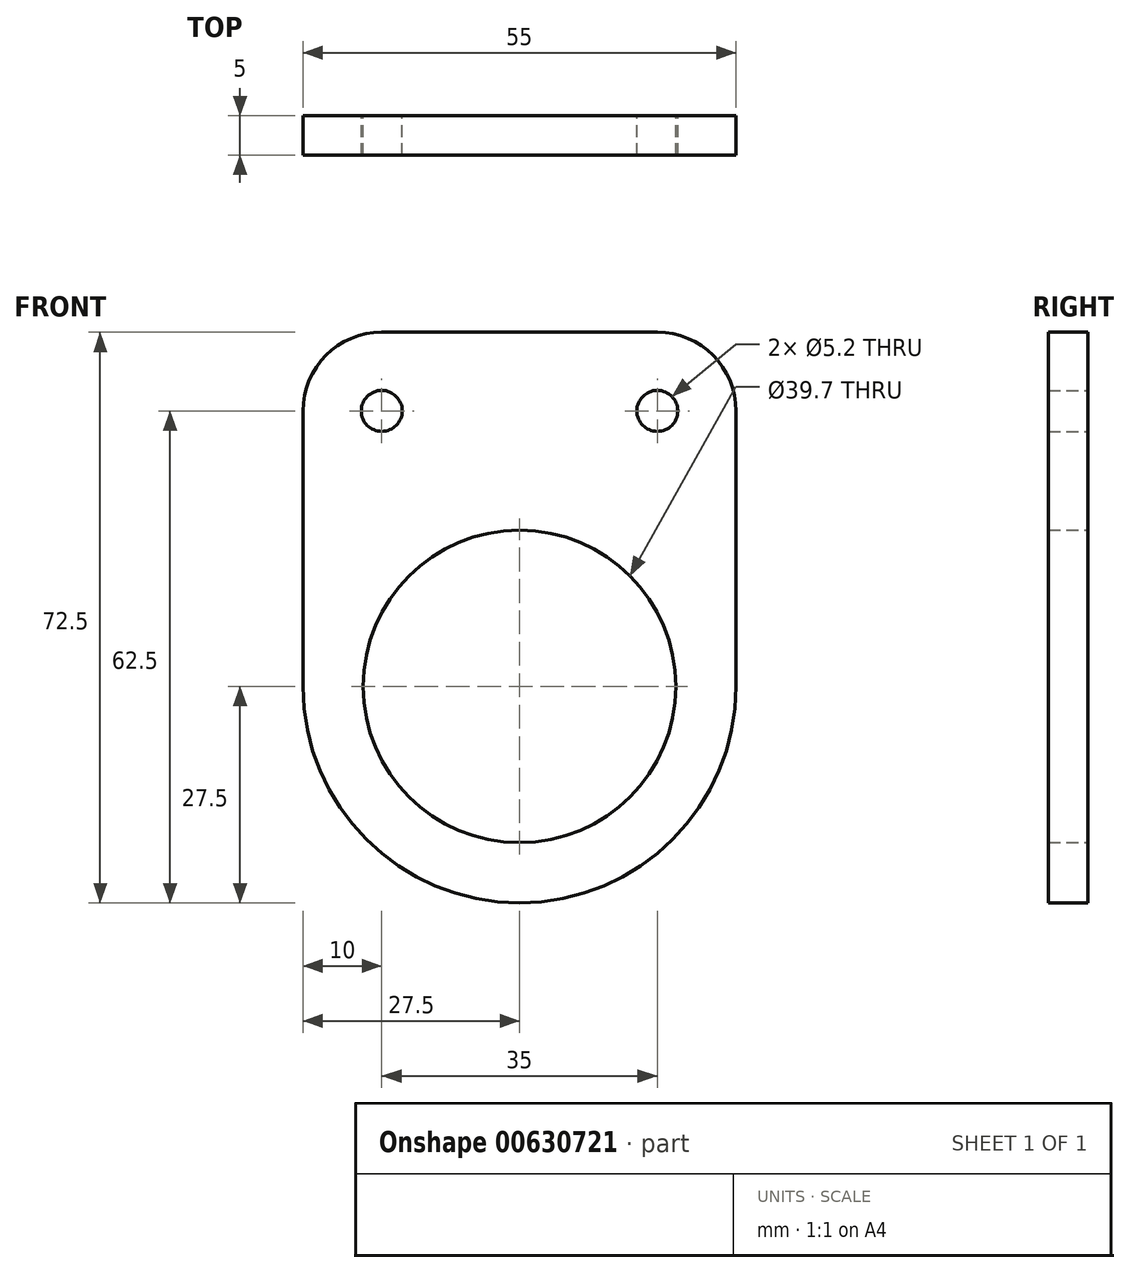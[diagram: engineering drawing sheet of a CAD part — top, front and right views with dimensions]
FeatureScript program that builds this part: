
annotation { "Feature Type Name" : "Feature", "Feature Type Description" : "" }
export const myFeature = defineFeature(function(context is Context, id is Id, definition is map)
    precondition{}
    {
        {
            var Q0;
            Q0=qCreatedBy(makeId("Front.planeOp"),FACE);
            var sketch = newSketch(context, id + "F0", { "sketchPlane" : qUnion([Q0])});
            skCircle(sketch, "E0", {"center": v(0, 0) * mm, "radius": 19.85 * mm});
            skArc(sketch, "E1", {"start": v(-27.5, 0) * mm, "mid": v(0, -27.5) * mm, "end": v(27.5, 0) * mm});
            skLineSegment(sketch, "E2.top", {"start": v(-17.5, 45) * mm, "end": v(17.5, 45) * mm});
            skLineSegment(sketch, "E2.left", {"start": v(-27.5, 0) * mm, "end": v(-27.5, 35) * mm});
            skLineSegment(sketch, "E2.right", {"start": v(27.5, 0) * mm, "end": v(27.5, 35) * mm});
            skLineSegment(sketch, "E3", {"start": v(-27.5, 35) * mm, "end": v(27.5, 35) * mm, "construction": true});
            skCircle(sketch, "E4", {"center": v(-17.5, 35) * mm, "radius": 2.6 * mm});
            skCircle(sketch, "E5", {"center": v(17.5, 35) * mm, "radius": 2.6 * mm});
            skPoint(sketch, "E6.visualSharp", {"position": v(-27.5, 45) * mm});
            skArc(sketch, "E6.filletArc", {"start": v(-17.5, 45) * mm, "mid": v(-24.57, 42.07) * mm, "end": v(-27.5, 35) * mm});
            skPoint(sketch, "E7.visualSharp", {"position": v(27.5, 45) * mm});
            skArc(sketch, "E7.filletArc", {"start": v(27.5, 35) * mm, "mid": v(24.57, 42.07) * mm, "end": v(17.5, 45) * mm});
            skLineSegment(sketch, "E8", {"start": v(-27.5, 25) * mm, "end": v(27.5, 25) * mm, "construction": true});
            skSolve(sketch);
        }
        {
            var Q0;
            Q0=makeQuery(id+"F0.imprint","IMPRINT",FACE,{"disambiguationData":[TD([[makeQuery(id+"F0.imprint","IMPRINT",EDGE,{"derivedFrom":sQuery(id+"F0.wireOp",EDGE,"E0")}),-1.0]])]});
            extrude(context, id + "F1", {"entities" : qUnion([Q0]), "depth" : 5 * mm, "offsetDistance" : 25 * mm});
        }
    });
